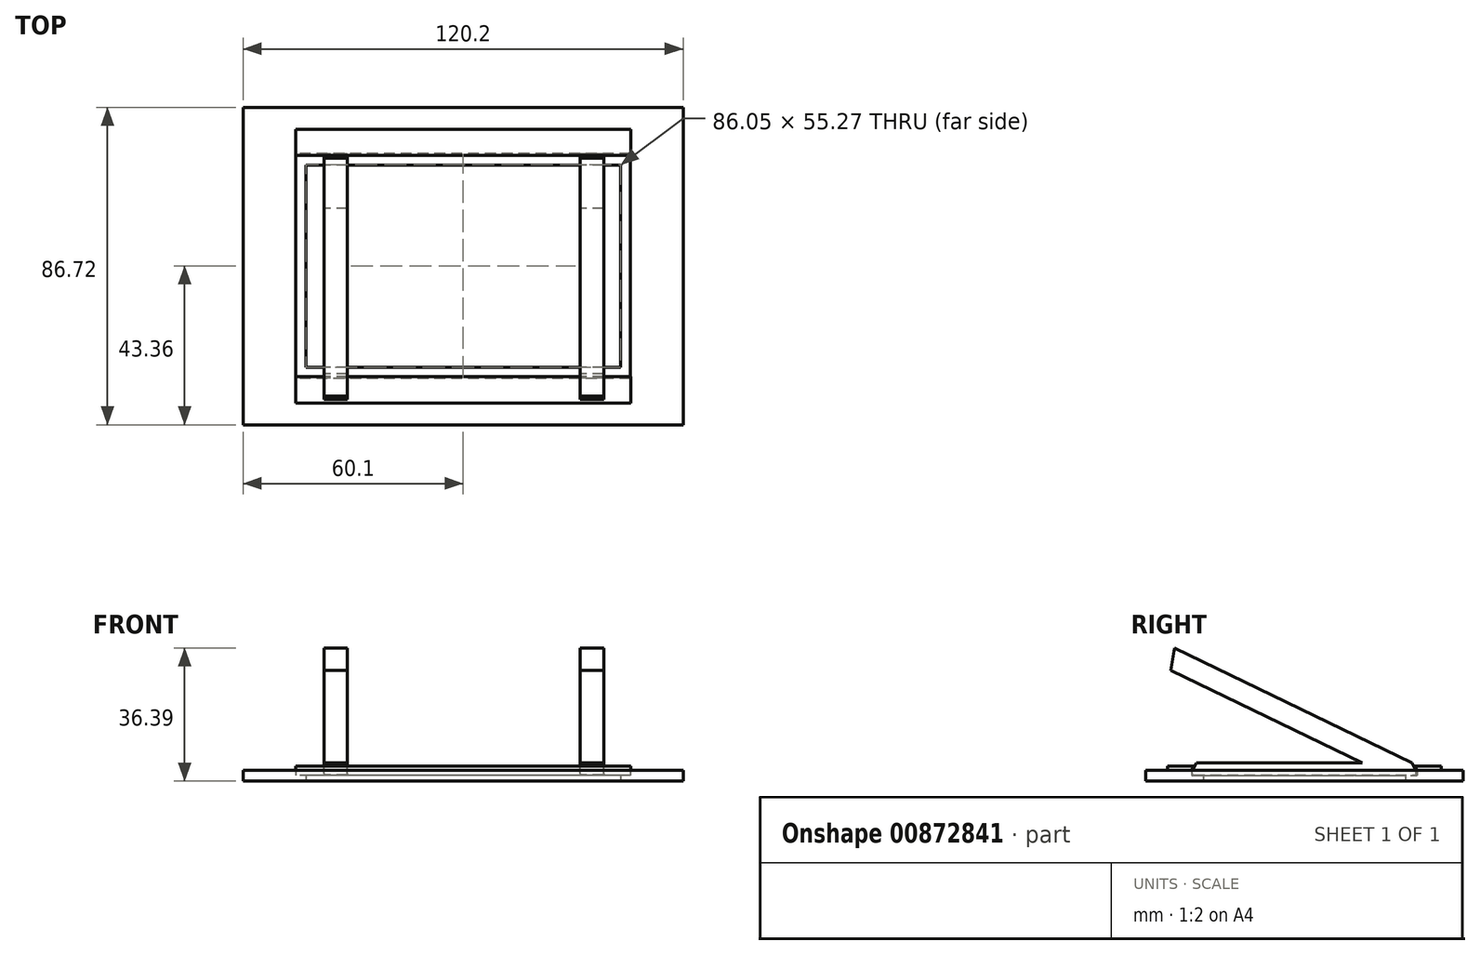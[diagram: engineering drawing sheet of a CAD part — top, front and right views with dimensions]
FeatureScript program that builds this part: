
annotation { "Feature Type Name" : "Feature", "Feature Type Description" : "" }
export const myFeature = defineFeature(function(context is Context, id is Id, definition is map)
    precondition{}
    {
        {
            var Q0;
            Q0=qCreatedBy(makeId("Top.planeOp"),FACE);
            var sketch = newSketch(context, id + "F0", { "sketchPlane" : qUnion([Q0])});
            skLineSegment(sketch, "E0.bottom", {"start": v(60.1, -43.36) * mm, "end": v(-60.1, -43.36) * mm});
            skLineSegment(sketch, "E0.top", {"start": v(60.1, 43.36) * mm, "end": v(-60.1, 43.36) * mm});
            skLineSegment(sketch, "E0.left", {"start": v(60.1, -43.36) * mm, "end": v(60.1, 43.36) * mm});
            skLineSegment(sketch, "E0.right", {"start": v(-60.1, -43.36) * mm, "end": v(-60.1, 43.36) * mm});
            skPoint(sketch, "E0.middle", {"position": v(0, 0) * mm});
            skLineSegment(sketch, "E1.bottom", {"start": v(45.72, -30.78) * mm, "end": v(-45.72, -30.78) * mm});
            skLineSegment(sketch, "E1.top", {"start": v(45.72, 30.78) * mm, "end": v(-45.72, 30.78) * mm});
            skLineSegment(sketch, "E1.left", {"start": v(45.72, -30.78) * mm, "end": v(45.72, 30.78) * mm});
            skLineSegment(sketch, "E1.right", {"start": v(-45.72, -30.78) * mm, "end": v(-45.72, 30.78) * mm});
            skLineSegment(sketch, "E2.bottom", {"start": v(43.03, -27.64) * mm, "end": v(-43.03, -27.64) * mm});
            skLineSegment(sketch, "E2.top", {"start": v(43.03, 27.64) * mm, "end": v(-43.03, 27.64) * mm});
            skLineSegment(sketch, "E2.left", {"start": v(43.03, -27.64) * mm, "end": v(43.03, 27.64) * mm});
            skLineSegment(sketch, "E2.right", {"start": v(-43.03, -27.64) * mm, "end": v(-43.03, 27.64) * mm});
            skSolve(sketch);
        }
        {
            var Q0;
            Q0=makeQuery(id+"F0.imprint","IMPRINT",FACE,{"disambiguationData":[TD([[makeQuery(id+"F0.imprint","IMPRINT",EDGE,{"derivedFrom":sQuery(id+"F0.wireOp",EDGE,"E0.bottom")}),-1.0]])]});
            extrude(context, id + "F1", {"entities" : qUnion([Q0]), "depth" : 3 * mm, "offsetDistance" : 25 * mm});
        }
        {
            var Q0;
            Q0=makeQuery(id+"F0.imprint","IMPRINT",FACE,{"disambiguationData":[TD([[makeQuery(id+"F0.imprint","IMPRINT",EDGE,{"derivedFrom":sQuery(id+"F0.wireOp",EDGE,"E1.bottom")}),-1.0]])]});
            extrude(context, id + "F2", {"entities" : qUnion([Q0]), "operationType" : NewBodyOperationType.ADD, "depth" : 1.6 * mm, "offsetDistance" : 25 * mm});
        }
        {
            var Q0;
            Q0=makeQuery(id+"F1.opExtrude","SWEPT_FACE",FACE,{"disambiguationData":[OSD([sQuery(id+"F0.wireOp",EDGE,"E1.right")])]});
            var sketch = newSketch(context, id + "F3", { "sketchPlane" : qUnion([Q0])});
            skLineSegment(sketch, "E3", {"start": v(30.78, 3) * mm, "end": v(30.24, 4.07) * mm});
            skLineSegment(sketch, "E4", {"start": v(30.24, 4.07) * mm, "end": v(37.4, 4.07) * mm});
            skLineSegment(sketch, "E5", {"start": v(37.4, 4.07) * mm, "end": v(37.4, 3) * mm});
            skLineSegment(sketch, "E6", {"start": v(37.4, 3) * mm, "end": v(30.78, 3) * mm});
            skLineSegment(sketch, "E7.MirrorCS", {"start": v(-30.24, 4.07) * mm, "end": v(-37.4, 4.07) * mm});
            skLineSegment(sketch, "E8.MirrorCS", {"start": v(-30.78, 3) * mm, "end": v(-30.24, 4.07) * mm});
            skLineSegment(sketch, "E9.MirrorCS", {"start": v(-37.4, 3) * mm, "end": v(-30.78, 3) * mm});
            skLineSegment(sketch, "E10.MirrorCS", {"start": v(-37.4, 4.07) * mm, "end": v(-37.4, 3) * mm});
            skSolve(sketch);
        }
        {
            var Q0;
            Q0 = qSketchRegion(id + "F3", true);
            extrude(context, id + "F4", {"entities" : qUnion([Q0]), "operationType" : NewBodyOperationType.ADD, "depth" : 91.5 * mm, "offsetDistance" : 25 * mm});
        }
        {
            var Q0;
            Q0=qCreatedBy(makeId("Right.planeOp"),FACE);
            var sketch = newSketch(context, id + "F5", { "sketchPlane" : qUnion([Q0])});
            skLineSegment(sketch, "E11", {"start": v(30.64, 1.7) * mm, "end": v(30.64, 2.7) * mm});
            skLineSegment(sketch, "E12", {"start": v(30.64, 2.7) * mm, "end": v(29.5, 4.97) * mm});
            skLineSegment(sketch, "E13.MirrorCS", {"start": v(-30.64, 2.7) * mm, "end": v(-29.5, 4.97) * mm});
            skLineSegment(sketch, "E14.MirrorCS", {"start": v(-30.64, 1.7) * mm, "end": v(-30.64, 2.7) * mm});
            skLineSegment(sketch, "E15", {"start": v(-30.64, 1.7) * mm, "end": v(30.64, 1.7) * mm});
            skLineSegment(sketch, "E16", {"start": v(29.5, 4.97) * mm, "end": v(-35.5, 36.39) * mm});
            skLineSegment(sketch, "E17", {"start": v(-36.43, 30.22) * mm, "end": v(15.81, 4.97) * mm});
            skLineSegment(sketch, "E18", {"start": v(-29.5, 4.97) * mm, "end": v(15.81, 4.97) * mm});
            skLineSegment(sketch, "E19", {"start": v(-35.5, 36.39) * mm, "end": v(-36.43, 30.22) * mm});
            skSolve(sketch);
        }
        {
            var Q0;
            Q0=makeQuery(id+"F5.imprint","IMPRINT",FACE,{"disambiguationData":[TD([[makeQuery(id+"F5.imprint","IMPRINT",EDGE,{"derivedFrom":sQuery(id+"F5.wireOp",EDGE,"E11")}),1.0]])]});
            extrude(context, id + "F6", {"entities" : qUnion([Q0]), "depth" : 6.4 * mm, "offsetDistance" : 25 * mm});
        }
        {
            var Q0;
            Q0=makeQuery(id+"F6.opExtrude","SWEPT_EDGE",EDGE,{"disambiguationData":[OSD([sQuery(id+"F5.wireOp",EDGE,"E11"),sQuery(id+"F5.wireOp",EDGE,"E15")])]});
            var Q1;
            Q1=makeQuery(id+"F6.opExtrude","SWEPT_EDGE",EDGE,{"disambiguationData":[OSD([sQuery(id+"F5.wireOp",EDGE,"E14.MirrorCS"),sQuery(id+"F5.wireOp",EDGE,"E15")])]});
            fillet(context, id + "F7", {"entities" : qUnion([Q0, Q1]), "radius" : 0.4 * mm, "tangentPropagation" : true, "allowEdgeOverflow" : false});
        }
        {
            var Q0;
            Q0=makeQuery(id+"F6.opExtrude","SWEPT_BODY",BODY,{"disambiguationData":[OSD([sQuery(id+"F5.wireOp",EDGE,"E11"),sQuery(id+"F5.wireOp",EDGE,"E12"),sQuery(id+"F5.wireOp",EDGE,"E13.MirrorCS"),sQuery(id+"F5.wireOp",EDGE,"E14.MirrorCS"),sQuery(id+"F5.wireOp",EDGE,"pcn6CaXG-zlKB-fqVR-FZnt-IwWtz3CLfqqX"),sQuery(id+"F5.wireOp",EDGE,"E15"),sQuery(id+"F5.wireOp",EDGE,"E16"),sQuery(id+"F5.wireOp",EDGE,"h7MVs4YR-U2M1-t3sq-SkPZ-XEsCe1RmFNez"),sQuery(id+"F5.wireOp",EDGE,"E17")])]});
            transform(context, id + "F8", {"entities" : qUnion([Q0]), "transformType" : TransformType.TRANSLATION_3D, "dx" : 32 * mm, "dy" : 0 * mm, "dz" : 0 * mm, "makeCopy" : true});
        }
        {
            var Q0;
            Q0=makeQuery(id+"F6.opExtrude","SWEPT_BODY",BODY,{"disambiguationData":[OSD([sQuery(id+"F5.wireOp",EDGE,"E11"),sQuery(id+"F5.wireOp",EDGE,"E12"),sQuery(id+"F5.wireOp",EDGE,"E13.MirrorCS"),sQuery(id+"F5.wireOp",EDGE,"E14.MirrorCS"),sQuery(id+"F5.wireOp",EDGE,"pcn6CaXG-zlKB-fqVR-FZnt-IwWtz3CLfqqX"),sQuery(id+"F5.wireOp",EDGE,"E15"),sQuery(id+"F5.wireOp",EDGE,"E16"),sQuery(id+"F5.wireOp",EDGE,"h7MVs4YR-U2M1-t3sq-SkPZ-XEsCe1RmFNez"),sQuery(id+"F5.wireOp",EDGE,"E17")])]});
            transform(context, id + "F9", {"entities" : qUnion([Q0]), "transformType" : TransformType.TRANSLATION_3D, "dx" : -38 * mm, "dy" : 0 * mm, "dz" : 0 * mm, "makeCopy" : false});
        }
    });
